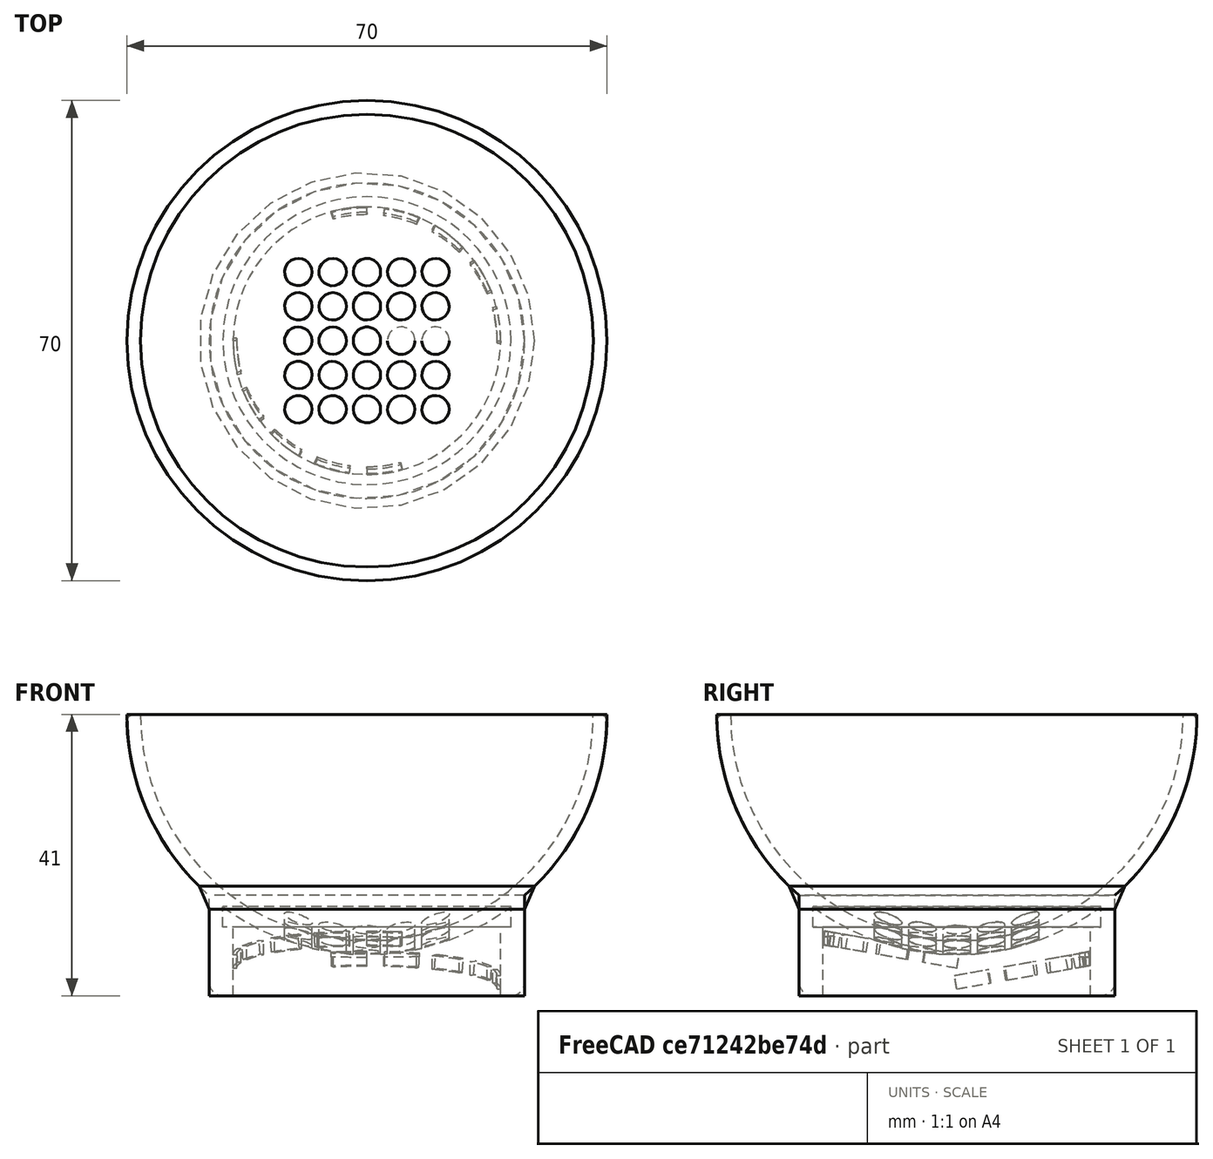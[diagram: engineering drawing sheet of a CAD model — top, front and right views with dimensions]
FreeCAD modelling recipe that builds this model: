
FCSTD DOCUMENT  (FreeCAD 0.15R4671 (Git))
Label: embudo_rosca
License: All rights reserved
LicenseURL: http://en.wikipedia.org/wiki/All_rights_reserved
objects: Part::Cylinder×10, Part::Cut×7, Part::FeaturePython×3, Part::MultiFuse×3, Part::Sphere×2, Part::Fillet×2, Part::Feature×1, Part::Chamfer×1
note: 29 computed .brp shape members not serialized (recipe doc carries the construction recipe); baked Part::Feature solids carry a one-line shape summary decoded from their .brp

FEATURE [Part::Cylinder] Cylinder  label="Cilindro"
  Angle = 360
  Height = 10
  Radius = 23
FEATURE [Part::Cylinder] Cylinder001  label="Cilindro001"
  Angle = 360
  Height = 29
  Placement = pos=(0,0,-2) rot=(0,0,1;0rad)
  Radius = 19.5
FEATURE [Part::Cut] Cut  label="base rosca"
  Base = -> Cylinder
  Tool = -> Cylinder001
FEATURE [Part::Cylinder] Cylinder004  label="Cilindro004"
  Angle = 15
  Height = 2
  Radius = 20
FEATURE [Part::Cylinder] Cylinder005  label="Cilindro005"
  Angle = 360
  Height = 2
  Radius = 19
FEATURE [Part::Cut] Cut004
  Base = -> Cylinder004
  Tool = -> Cylinder005
FEATURE [Part::FeaturePython] Array001  label="fijacion1 rosca"  # Draft array (typed FeaturePython)
  Angle = 90
  ArrayType = 1
  Axis = (0,0,1)
  Base = -> Cut004
  Center = (0,0,0)
  Fuse = false
  IntervalAxis = (0,0,0)
  IntervalX = (1,0,0)
  IntervalY = (0,1,0)
  IntervalZ = (0,0,0)
  NumberPolar = 5
  NumberX = 0
  NumberY = 0
  NumberZ = 0
  Placement = pos=(0,0,1) rot=(1,0,0;0.174533rad)
FEATURE [Part::Cylinder] Cylinder011  label="Cilindro011"
  Angle = 15
  Height = 2
  Placement = pos=(0,0,0) rot=(0,0,1;3.14159rad)
  Radius = 20
FEATURE [Part::Cylinder] Cylinder012  label="Cilindro012"
  Angle = 180
  Height = 2
  Placement = pos=(0,0,0) rot=(0,0,1;3.14159rad)
  Radius = 19
FEATURE [Part::Cut] Cut006
  Base = -> Cylinder011
  Tool = -> Cylinder012
FEATURE [Part::FeaturePython] Array002  label="fijacion2 rosca"  # Draft array (typed FeaturePython)
  Angle = 90
  ArrayType = 1
  Axis = (0,0,1)
  Base = -> Cut006
  Center = (0,0,0)
  Fuse = false
  IntervalAxis = (0,0,0)
  IntervalX = (1,0,0)
  IntervalY = (0,1,0)
  IntervalZ = (0,0,0)
  NumberPolar = 5
  NumberX = 0
  NumberY = 0
  NumberZ = 0
  Placement = pos=(0,0,4) rot=(-1,0,0;0.174533rad)
FEATURE [Part::MultiFuse] Fusion  label="rosca"
  Shapes = -> [Array001,Array002,Cut]
FEATURE [Part::Cylinder] Cylinder013  label="Cilindro013"
  Angle = 360
  Height = 5
  Placement = pos=(0,0,10) rot=(0,0,1;0rad)
  Radius = 23
FEATURE [Part::Cylinder] Cylinder014  label="Cilindro014"
  Angle = 360
  Height = 5
  Placement = pos=(0,0,10) rot=(0,0,1;0rad)
  Radius = 21
FEATURE [Part::Cut] Cut007  label="fijacion rosca+parte superior"
  Base = -> Cylinder013
  Tool = -> Cylinder014
FEATURE [Part::Sphere] Sphere  label="Esfera"
  Angle1 = -90
  Angle2 = 0
  Angle3 = 360
  Placement = pos=(0,0,24) rot=(0,0,1;0rad)
  Radius = 35
FEATURE [Part::Sphere] Sphere001  label="Esfera001"
  Angle1 = -90
  Angle2 = 0
  Angle3 = 360
  Placement = pos=(0,0,24) rot=(0,0,1;0rad)
  Radius = 33
FEATURE [Part::Cut] Cut008
  Base = -> Sphere
  Placement = pos=(0,0,2) rot=(0,0,1;0rad)
  Tool = -> Sphere001
FEATURE [Part::Cylinder] Cylinder015  label="Cilindro015"
  Angle = 360
  Height = 10
  Radius = 2
FEATURE [Part::Cut] Cut009  label="embudo superior"
  Base = -> Cut008
  Placement = pos=(0,0,15) rot=(0,0,1;0rad)
  Tool = -> Cylinder015
FEATURE [Part::Cylinder] Cylinder016  label="Cilindro016"
  Angle = 360
  Height = 9
  Placement = pos=(0,0,5) rot=(0,0,1;0rad)
  Radius = 2
FEATURE [Part::FeaturePython] Array003  label="orificios escurridor"  # Draft array (typed FeaturePython)
  Angle = 360
  ArrayType = 0
  Axis = (0,0,1)
  Base = -> Cylinder016
  Center = (0,0,0)
  Fuse = false
  IntervalAxis = (0,0,0)
  IntervalX = (5,0,0)
  IntervalY = (0,5,0)
  IntervalZ = (0,0,0)
  NumberPolar = 6
  NumberX = 5
  NumberY = 5
  NumberZ = 1
  Placement = pos=(-10,-10,0) rot=(0,0,1;0rad)
FEATURE [Part::MultiFuse] Fusion001  label="embudo rosca final partes"
  Shapes = -> [Fusion,Cut007]
FEATURE [Part::Cut] Cut010  label="embudo superior001"
  Base = -> Cut009
  Tool = -> Array003
FEATURE [Part::MultiFuse] Fusion002  label="union de piezas"
  Shapes = -> [Cut010,Fusion001]
FEATURE [Part::Feature] Fusion002001  label="Fusion003"
  shape: bbox 70 x 70 x 41 mm, 90 faces (baked)
FEATURE [Part::Chamfer] Chamfer
  Base = -> Fusion002001
  Edges = 1 edges r=2: [Edge91]
FEATURE [Part::Fillet] Fillet
  Base = -> Chamfer
  Edges = 1 edges r=2: [Edge8]
FEATURE [Part::Fillet] Fillet001  label="embudo final redondeado"
  Base = -> Fillet
  Edges = 1 edges r=1: [Edge10]
